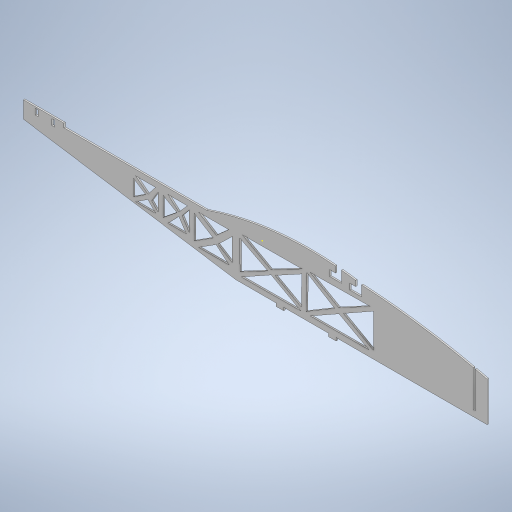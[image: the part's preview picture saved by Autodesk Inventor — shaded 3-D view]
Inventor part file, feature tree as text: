
AUTODESK INVENTOR PART (.ipt)
format: ipt  version: 2024 (Build 280153000, 153)  size: 364,032 bytes
history: native  units: mm
features: sketch x2, extrude x1
ambient origin geometry x8: Origin, YZ Plane, XZ Plane, XY Plane, X Axis, Y Axis, Z Axis, Center Point
bodies: Solid1 (feature_tree)
feature tree (3):
  extrude  "Extrusion1"  [1 undecoded]
  sketch  "Sketch2"
  sketch  "Sketch1"  dims[d0=2.5mm d1=0.0mm]
note: 1 required parameter value undecoded (feature->parameter linkage not recoverable at this tier; creation-order binding heuristic only, values carry confidence <= 0.55)
